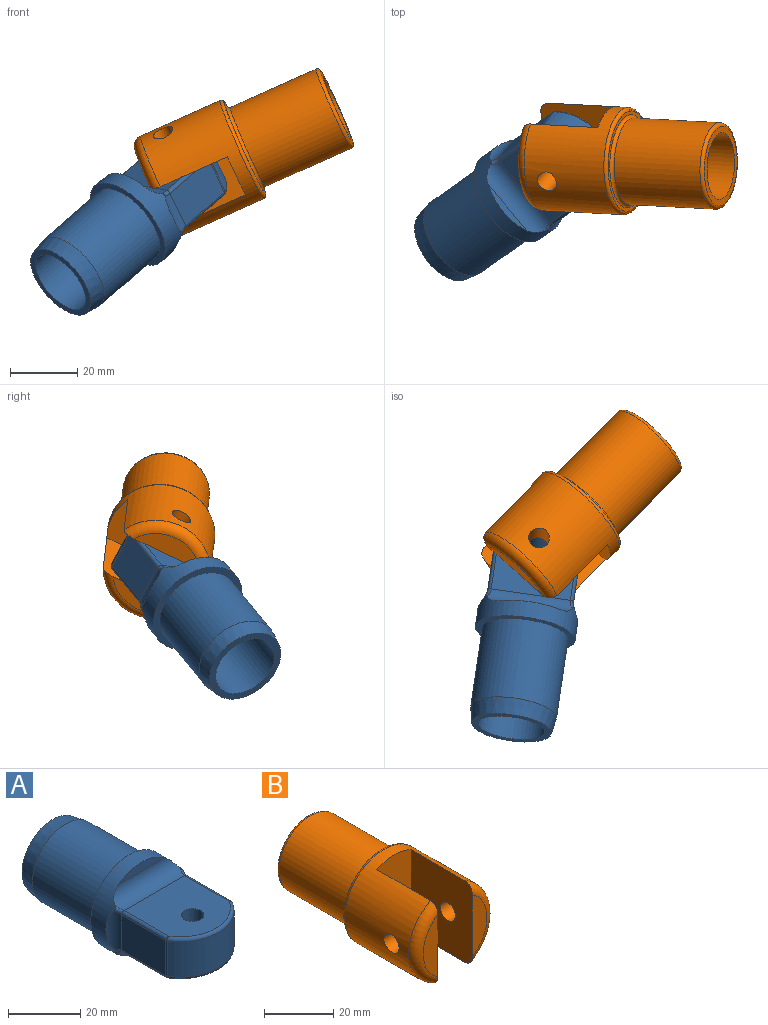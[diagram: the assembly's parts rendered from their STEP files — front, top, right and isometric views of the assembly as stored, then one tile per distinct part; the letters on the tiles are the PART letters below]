
ASSEMBLY  parts=2 mates=1
PART A: 35 faces, bbox 30x66.2x30 mm
  f0: cylinder r=12.9mm len=25.8mm, axis (0,-1,0), area 2026.3mm2, adj f2,f10
  f1: plane 24.04x24.04mm, normal (0,1,0), area 139.6mm2, adj f2,f3
  f2: cone r=12.9mm half-angle=10deg, axis (0,-1,0), area 397.5mm2, adj f0,f1
  f3: cylinder r=10mm len=30mm, axis (0,1,0), area 1885mm2, adj f1,f18
  f4: cylinder r=5mm len=13.31mm, axis (0,0,1), area 52.5mm2, adj f11,f15,f19,f24
  f5: cylinder r=5mm len=13.31mm, axis (0,0,-1), area 52.5mm2, adj f11,f12,f20,f27
  f6: cylinder r=5mm len=25.66mm, axis (1,0,0), area 179.6mm2, adj f11,f13,f16,f19,f20
  f7: cylinder r=5mm len=25.66mm, axis (-1,0,0), area 179.6mm2, adj f11,f14,f17,f24,f27
  f8: cylinder r=3.1mm len=14mm, axis (0,0,-1), area 272.7mm2, adj f13,f14
  f9: cylinder r=15mm len=25.5mm, axis (0,0,-1), area 365.8mm2, adj f22,f29,f30,f34
  f10: plane 30x30mm, normal (0,1,0), area 184.1mm2, adj f0,f11
  f11: cylinder r=15mm len=30mm, axis (0,1,0), area 537.7mm2, adj f4,f5,f6,f7,f10,f16,f17,f19
  f12: plane 17.38x12mm, normal (-1,0,0), area 208.5mm2, adj f5,f23,f30,f31
  f13: plane 24x23.8mm, normal (0,0,-1), area 494.7mm2, adj f6,f8,f21,f22,f23
  f14: plane 24x23.8mm, normal (0,0,1), area 494.7mm2, adj f7,f8,f28,f31,f34
  f15: plane 17.38x12mm, normal (1,0,0), area 208.5mm2, adj f4,f21,f28,f29
  f16: plane 18x3mm, normal (0,-1,0), area 36.8mm2, adj f6,f11
  f17: plane 18x3mm, normal (0,-1,0), area 36.8mm2, adj f7,f11
  f18: plane 20x20mm, normal (0,1,0), area 314.2mm2, adj f3
  f19: bspline ~3.57x1.93mm, area 3.9mm2, adj f4,f6,f11,f21
  f20: bspline ~3.57x1.93mm, area 3.9mm2, adj f5,f6,f11,f23
  f21: cylinder r=1mm len=17.38mm, axis (0,1,0), area 27.3mm2, adj f13,f15,f19,f25
  f22: torus R=14mm, axis (0,0,-1), area 46.7mm2, adj f9,f13,f25,f26
  f23: cylinder r=1mm len=17.38mm, axis (0,-1,0), area 27.3mm2, adj f12,f13,f20,f26
  f24: bspline ~3.57x1.93mm, area 3.9mm2, adj f4,f7,f11,f28
  f25: sphere r=1mm, area 0.6mm2, adj f21,f22,f29
  f26: sphere r=1mm, area 0.6mm2, adj f22,f23,f30
  f27: bspline ~3.57x1.93mm, area 3.9mm2, adj f5,f7,f11,f31
  f28: cylinder r=1mm len=17.38mm, axis (0,-1,0), area 27.3mm2, adj f14,f15,f24,f32
  f29: cylinder r=1mm len=12mm, axis (0,0,-1), area 6.7mm2, adj f9,f15,f25,f32
  f30: cylinder r=1mm len=12mm, axis (0,0,-1), area 6.7mm2, adj f9,f12,f26,f33
  f31: cylinder r=1mm len=17.38mm, axis (0,1,0), area 27.3mm2, adj f12,f14,f27,f33
  f32: sphere r=1mm, area 0.6mm2, adj f28,f29,f34
  f33: sphere r=1mm, area 0.6mm2, adj f30,f31,f34
  f34: torus R=14mm, axis (0,0,-1), area 46.7mm2, adj f9,f14,f32,f33
PART B: 18 faces, bbox 34.6x60x34.6 mm
  f0: plane 21.91x6mm, normal (0,-1,0), area 92.7mm2, adj f9,f15
  f1: cylinder r=3.1mm len=9mm, axis (1,0,0), area 172.4mm2, adj f5,f15
  f2: torus R=13mm, axis (0,-1,0), area 152mm2, adj f5,f6,f16
  f3: cylinder r=12.9mm len=28mm, axis (0,-1,0), area 2269.5mm2, adj f11,f12
  f4: plane 23.8x23.8mm, normal (0,1,0), area 130.7mm2, adj f11,f13
  f5: cylinder r=16mm len=32mm, axis (0,1,0), area 1915.5mm2, adj f1,f2,f8,f9,f10,f15,f16,f17
  f6: plane 21.91x6mm, normal (0,-1,0), area 92.7mm2, adj f2,f16
  f7: plane 30x30mm, normal (0,1,0), area 99.9mm2, adj f10,f12
  f8: cylinder r=3.1mm len=9mm, axis (1,0,0), area 172.4mm2, adj f5,f16
  f9: torus R=13mm, axis (0,-1,0), area 152mm2, adj f0,f5,f15
  f10: torus R=15mm, axis (0,-1,0), area 154.3mm2, adj f5,f7
  f11: torus R=11.9mm, axis (0,-1,0), area 123.7mm2, adj f3,f4
  f12: torus R=13.9mm, axis (0,-1,0), area 130.9mm2, adj f3,f7
  f13: cylinder r=10mm len=25mm, axis (0,1,0), area 1570.8mm2, adj f4,f14
  f14: plane 20x20mm, normal (0,1,0), area 314.2mm2, adj f13
  f15: plane 28.78x25mm, normal (-1,0,0), area 684.8mm2, adj f0,f1,f5,f9,f17
  f16: plane 28.78x25mm, normal (1,0,0), area 684.8mm2, adj f2,f5,f6,f8,f17
  f17: plane 32x14mm, normal (0,-1,0), area 433.3mm2, adj f5,f15,f16
PLACE A rot(axis=(-0.09,-0.33,0.94),130.6deg) t=(35.79,-37.65,1.81)mm
PLACE B rot(axis=(0.78,0.57,-0.28),123deg) t=(70.69,-26.82,24.37)mm
MATE revolute B.f1 <-> A.f8  axis (0.39,0.44,-0.81) through (49.75,-28.94,21.89)mm
